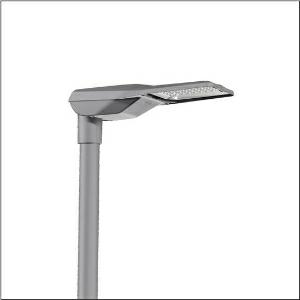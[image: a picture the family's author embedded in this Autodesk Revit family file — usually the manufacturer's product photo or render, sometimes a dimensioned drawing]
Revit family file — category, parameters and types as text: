
# Revit family: streetlight_sl_21_iq_mini___st1_0a_5xe2d41g08hb_63a2
name_source: partatom
category: Lighting Fixtures
units: mm (PartAtom-declared; Revit-internal decimal feet)

## family parameters
Cut with Voids When Loaded = No
Host = Face
Light Source = No
Part Type = Normal
Room Calculation Point = No
Round Connector Dimension = Use Diameter
Shared = No

## types (1)
- --- (1 x LED, 9860 lm, 70.9 W, 4000K)
    Apparent Load = 71 VA
    CIE Flux Codes = 37 72 97 100 100
    Color Rendering = 70
    Color Temperature = 4000K
    Default Elevation = 1800 mm
    Description = Streetlight SL 21 iQ mini, mast luminaire, primary light control with lens, of PMMA, primary optical cover: cover, of toughened safety glass, transparent, light distribution: ST1.0a, light emission: direct distribution, primary light characteristic: asymmetric, installation type: post-top, side-entry, LED, High Power LED, rated luminous flux: 9.860lm, luminous efficacy: 139lm/W, light colour: 740, colour temperature: 4000K, control gear: iQ Street-Remote, control: Street-Remote, Auto-Match, Temp-Guard, Lumen-Switch, Night-Set, Smart-Wire, Light-Fading, Desk-Remote (wireless, voltage-free reading and setting of iQ features in the workshop via application-optimized NFC function/RFID function), optimised constant luminous flux control (CLO 2.0), pre-setting: linear dimming characteristic, mains connection: 220..240V, AC, 50/60Hz, start of lifetime: 71W, end of service life: 75W, reduction: 31W, luminaire housing, of diecast aluminium, powder-coated, SITECO metallic grey (DB 702S), corrosivity category C5 high according to DIN EN ISO 12944, please order mast flange separately, inclination adjustable: 0°, 5°, 10°, 15°, sealing non-destructively replaceable, multi-level sealing system, length: 628mm, width: 235mm, height: 110mm, mast flange for spigot size: 42mm (side-entry): 5XC10008XM4, 60/48mm (side-entry/post-top): 5XC10108XM2, 76/60mm (side-entry/post-top): 5XC10108XM1, mounting height: 4..8m, protection rating (complete): IP66, insulation class (complete): insulation class II (safety insulation), certification: CE, ENEC, ENEC+, VDE, impact resistance: IK10, permissible operating ambient temperature for outdoor applications: -40..+50°C, standard-compliant lighting for roads and squares, packaging unit: 1 piece

Light Distribution: ST1.0a
    Height = 110 mm
    Lamp = 1 x LED
    Lamp Light Flux = 9860 lm
    Lamp Power = 70.9 W
    Lamp count = 1
    Length = 625 mm
    Luminous efficacy = 139 lm/W
    Manufacturer = Siteco
    ModVariant = No
    Model = 5XE2D41G08HB
    Number of Poles = 1
    OnlyDefault = Yes
    Power Factor = 1
    Product Name = Streetlight SL 21 iQ mini | ST1.0a
    Product group = mast luminaire | pylon top
    ProductGroupID = 6100
    Protection Class = Protection class II
    Protection Degree = IP 66
    RLX_Detail_Level = 1
    RLX_Emergency_Light_Flux = 0 lm
    RLX_Emergency_Type = 0
    RLX_Emergency_Type_DB = No
    RlxData = <blob elided: 26293 chars, md5=5135cc95>
    Socket = socket
    Standby Power = 0 W
    System Light Flux = 9860 lm
    System Power = 71 W
    Type Comments = factory setting: luminous flux: 100 % | dim-lin: 254 | 711 mA
    Type Image = l_1003519.jpg
    URL = http://relux.com
    VarID = @adj_157527
    Voltage = 0 V
    Weight = 0.00 kg
    Width = 234 mm

## geometry (parser evidence)
native form markers: Blend x4, Sweep x12
no freeform markers — native parametric forms only
